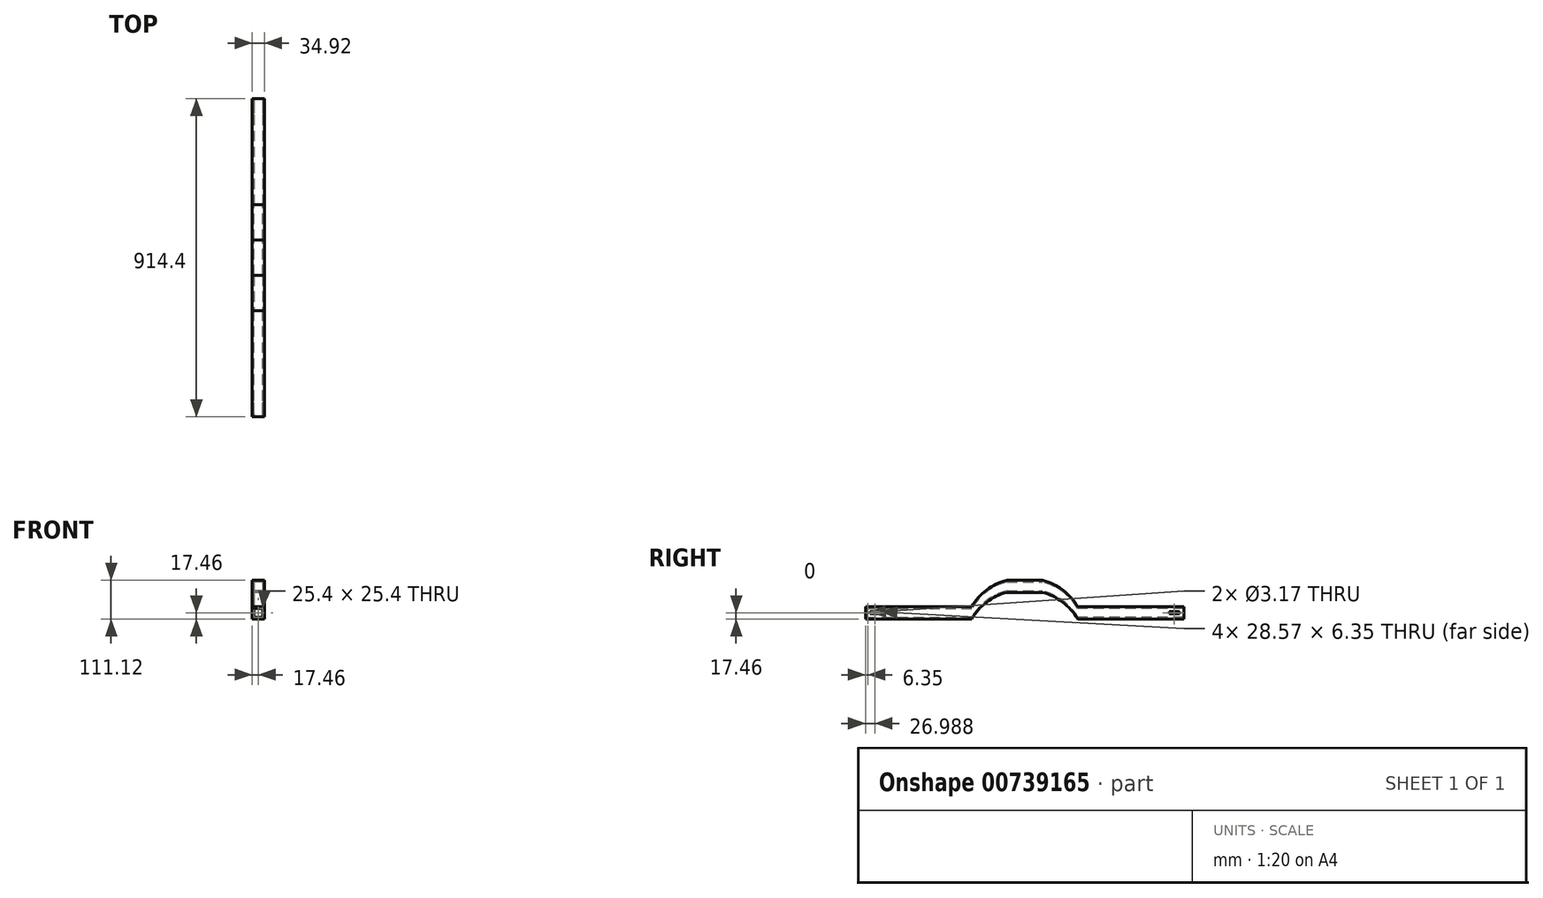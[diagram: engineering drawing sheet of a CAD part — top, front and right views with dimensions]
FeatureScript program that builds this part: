
annotation { "Feature Type Name" : "Feature", "Feature Type Description" : "" }
export const myFeature = defineFeature(function(context is Context, id is Id, definition is map)
    precondition{}
    {
        {
            var Q0;
            Q0=qCreatedBy(makeId("Front.planeOp"),FACE);
            var sketch = newSketch(context, id + "F0", { "sketchPlane" : qUnion([Q0])});
            skLineSegment(sketch, "E0.bottom", {"start": v(-17.46, -17.46) * mm, "end": v(17.46, -17.46) * mm});
            skLineSegment(sketch, "E0.top", {"start": v(-17.46, 17.46) * mm, "end": v(17.46, 17.46) * mm});
            skLineSegment(sketch, "E0.left", {"start": v(-17.46, -17.46) * mm, "end": v(-17.46, 17.46) * mm});
            skLineSegment(sketch, "E0.right", {"start": v(17.46, -17.46) * mm, "end": v(17.46, 17.46) * mm});
            skPoint(sketch, "E0.middle", {"position": v(0, 0) * mm});
            skLineSegment(sketch, "E1.bottom", {"start": v(-12.7, -12.7) * mm, "end": v(12.7, -12.7) * mm});
            skLineSegment(sketch, "E1.top", {"start": v(-12.7, 12.7) * mm, "end": v(12.7, 12.7) * mm});
            skLineSegment(sketch, "E1.left", {"start": v(-12.7, -12.7) * mm, "end": v(-12.7, 12.7) * mm});
            skLineSegment(sketch, "E1.right", {"start": v(12.7, -12.7) * mm, "end": v(12.7, 12.7) * mm});
            skSolve(sketch);
        }
        {
            var Q0;
            Q0 = qSketchRegion(id + "F0", true);
            extrude(context, id + "F1", {"entities" : qUnion([Q0]), "depth" : 50.8 * mm, "offsetDistance" : 25.4 * mm});
        }
        {
            var Q0;
            Q0=qCreatedBy(makeId("Right.planeOp"),FACE);
            var sketch = newSketch(context, id + "F2", { "sketchPlane" : qUnion([Q0])});
            skArc(sketch, "E2", {"start": v(101.6, -76.2) * mm, "mid": v(58.36, -28.01) * mm, "end": v(0, 0) * mm});
            skSolve(sketch);
        }
        {
            var Q0;
            Q0=makeQuery(id+"F1.opExtrude","CAP_FACE",FACE,{"disambiguationData":[OSD([sQuery(id+"F0.wireOp",EDGE,"E0.bottom"),sQuery(id+"F0.wireOp",EDGE,"E0.top"),sQuery(id+"F0.wireOp",EDGE,"E0.left"),sQuery(id+"F0.wireOp",EDGE,"E0.right"),sQuery(id+"F0.wireOp",EDGE,"E1.bottom"),sQuery(id+"F0.wireOp",EDGE,"E1.top"),sQuery(id+"F0.wireOp",EDGE,"E1.left"),sQuery(id+"F0.wireOp",EDGE,"E1.right")])],"isStart":true});
            var Q1;
            Q1=sQuery(id+"F2.wireOp",EDGE,"E2");
            sweep(context, id + "F3", {"operationType" : NewBodyOperationType.ADD, "profiles" : qUnion([Q0]), "path" : qUnion([Q1]), "keepProfileOrientation" : true});
        }
        {
            var Q0;
            Q0=makeQuery(id+"F3.opSweep","CAP_FACE",FACE,{"disambiguationData":[OSD([sQuery(id+"F0.wireOp",EDGE,"E0.bottom"),sQuery(id+"F0.wireOp",EDGE,"E0.top"),sQuery(id+"F0.wireOp",EDGE,"E0.left"),sQuery(id+"F0.wireOp",EDGE,"E0.right"),sQuery(id+"F0.wireOp",EDGE,"E1.bottom"),sQuery(id+"F0.wireOp",EDGE,"E1.top"),sQuery(id+"F0.wireOp",EDGE,"E1.left"),sQuery(id+"F0.wireOp",EDGE,"E1.right"),sQuery(id+"F2.wireOp",VERTEX,"E2.start")])],"isStart":false});
            var sketch = newSketch(context, id + "F4", { "sketchPlane" : qUnion([Q0])});
            skSolve(sketch);
        }
        {
            var Q0;
            {var subQ0=sQuery(id+"F2.wireOp",VERTEX,"E2.start");Q0=makeQuery(id+"F4.imprint","IMPRINT",FACE,{"disambiguationData":[TD([[makeQuery(id+"F4.imprint","IMPRINT",EDGE,{"derivedFrom":makeQuery(id+"F3.opSweep","CAP_EDGE",EDGE,{"disambiguationData":[OSD([sQuery(id+"F0.wireOp",EDGE,"E0.bottom"),subQ0])],"isStart":false})}),-1.0]])]});}
            extrude(context, id + "F5", {"entities" : qUnion([Q0]), "operationType" : NewBodyOperationType.ADD, "depth" : 304.8 * mm, "offsetDistance" : 25.4 * mm});
        }
        {
            var Q0;
            {var subQ0=sQuery(id+"F0.wireOp",EDGE,"E0.left");Q0=makeQuery(id+"F5.boolean.opBoolean","MERGE",FACE,{"derivedFrom":[makeQuery(id+"F3.boolean.opBoolean","MERGE",FACE,{"derivedFrom":[makeQuery(id+"F1.opExtrude","SWEPT_FACE",FACE,{"disambiguationData":[OSD([subQ0])]}),makeQuery(id+"F3.opSweep","SWEPT_FACE",FACE,{"disambiguationData":[OSD([subQ0,sQuery(id+"F2.wireOp",EDGE,"E2")])]})]}),makeQuery(id+"F5.opExtrude","SWEPT_FACE",FACE,{"disambiguationData":[OSD([subQ0,sQuery(id+"F2.wireOp",VERTEX,"E2.start")])]})]});}
            var sketch = newSketch(context, id + "F6", { "sketchPlane" : qUnion([Q0])});
            skLineSegment(sketch, "E3.bottom", {"start": v(-365.12, -73.02) * mm, "end": v(-393.7, -73.02) * mm});
            skLineSegment(sketch, "E3.top", {"start": v(-365.12, -79.37) * mm, "end": v(-393.7, -79.37) * mm});
            skLineSegment(sketch, "E3.left", {"start": v(-365.12, -73.02) * mm, "end": v(-365.12, -79.37) * mm});
            skLineSegment(sketch, "E3.right", {"start": v(-393.7, -73.02) * mm, "end": v(-393.7, -79.37) * mm});
            skPoint(sketch, "E3.middle", {"position": v(-379.41, -76.2) * mm});
            skPoint(sketch, "E3.middle.positionSnap0", {"position": v(-406.4, -76.2) * mm});
            skPoint(sketch, "E3.centerSnap0", {"position": v(-406.4, -76.2) * mm});
            skSolve(sketch);
        }
        {
            var Q0;
            Q0 = qSketchRegion(id + "F6", true);
            extrude(context, id + "F7", {"entities" : qUnion([Q0]), "operationType" : NewBodyOperationType.REMOVE, "depth" : 25.4 * mm, "offsetDistance" : 25.4 * mm, "hasSecondDirection" : true, "secondDirectionOppositeDirection" : true, "secondDirectionDepth" : 59.44 * mm});
        }
        {
            var Q0;
            Q0=makeQuery(id+"F1.opExtrude","SWEPT_BODY",BODY,{"disambiguationData":[OSD([sQuery(id+"F0.wireOp",EDGE,"E0.bottom"),sQuery(id+"F0.wireOp",EDGE,"E0.top"),sQuery(id+"F0.wireOp",EDGE,"E0.left"),sQuery(id+"F0.wireOp",EDGE,"E0.right"),sQuery(id+"F0.wireOp",EDGE,"E1.bottom"),sQuery(id+"F0.wireOp",EDGE,"E1.top"),sQuery(id+"F0.wireOp",EDGE,"E1.left"),sQuery(id+"F0.wireOp",EDGE,"E1.right")])]});
            var Q1;
            Q1=makeQuery(id+"F1.opExtrude","CAP_FACE",FACE,{"disambiguationData":[OSD([sQuery(id+"F0.wireOp",EDGE,"E0.bottom"),sQuery(id+"F0.wireOp",EDGE,"E0.top"),sQuery(id+"F0.wireOp",EDGE,"E0.left"),sQuery(id+"F0.wireOp",EDGE,"E0.right"),sQuery(id+"F0.wireOp",EDGE,"E1.bottom"),sQuery(id+"F0.wireOp",EDGE,"E1.top"),sQuery(id+"F0.wireOp",EDGE,"E1.left"),sQuery(id+"F0.wireOp",EDGE,"E1.right")])],"isStart":false});
            mirror(context, id + "F8", {"operationType" : NewBodyOperationType.ADD, "entities" : qUnion([Q0]), "mirrorPlane" : qUnion([Q1])});
        }
        {
            var Q0;
            {var subQ0=sQuery(id+"F0.wireOp",EDGE,"E0.left");var subQ1=makeQuery(id+"F5.boolean.opBoolean","MERGE",FACE,{"derivedFrom":[makeQuery(id+"F3.boolean.opBoolean","MERGE",FACE,{"derivedFrom":[makeQuery(id+"F1.opExtrude","SWEPT_FACE",FACE,{"disambiguationData":[OSD([subQ0])]}),makeQuery(id+"F3.opSweep","SWEPT_FACE",FACE,{"disambiguationData":[OSD([subQ0,sQuery(id+"F2.wireOp",EDGE,"E2")])]})]}),makeQuery(id+"F5.opExtrude","SWEPT_FACE",FACE,{"disambiguationData":[OSD([subQ0,sQuery(id+"F2.wireOp",VERTEX,"E2.start")])]})]});Q0=makeQuery(id+"F8.boolean.opBoolean","MERGE",FACE,{"derivedFrom":[subQ1,makeQuery(id+"F8.opPattern","COPY",FACE,{"derivedFrom":subQ1,"instanceName":"1"})]});}
            var sketch = newSketch(context, id + "F9", { "sketchPlane" : qUnion([Q0])});
            skCircle(sketch, "E4", {"center": v(501.65, -76.2) * mm, "radius": 1.59 * mm});
            skPoint(sketch, "E4.centerSnap0", {"position": v(495.3, -76.2) * mm});
            skSolve(sketch);
        }
        {
            var Q0;
            Q0 = qSketchRegion(id + "F9", true);
            extrude(context, id + "F10", {"entities" : qUnion([Q0]), "operationType" : NewBodyOperationType.REMOVE, "oppositeDirection" : true, "depth" : 50.04 * mm, "offsetDistance" : 25.4 * mm});
        }
    });
